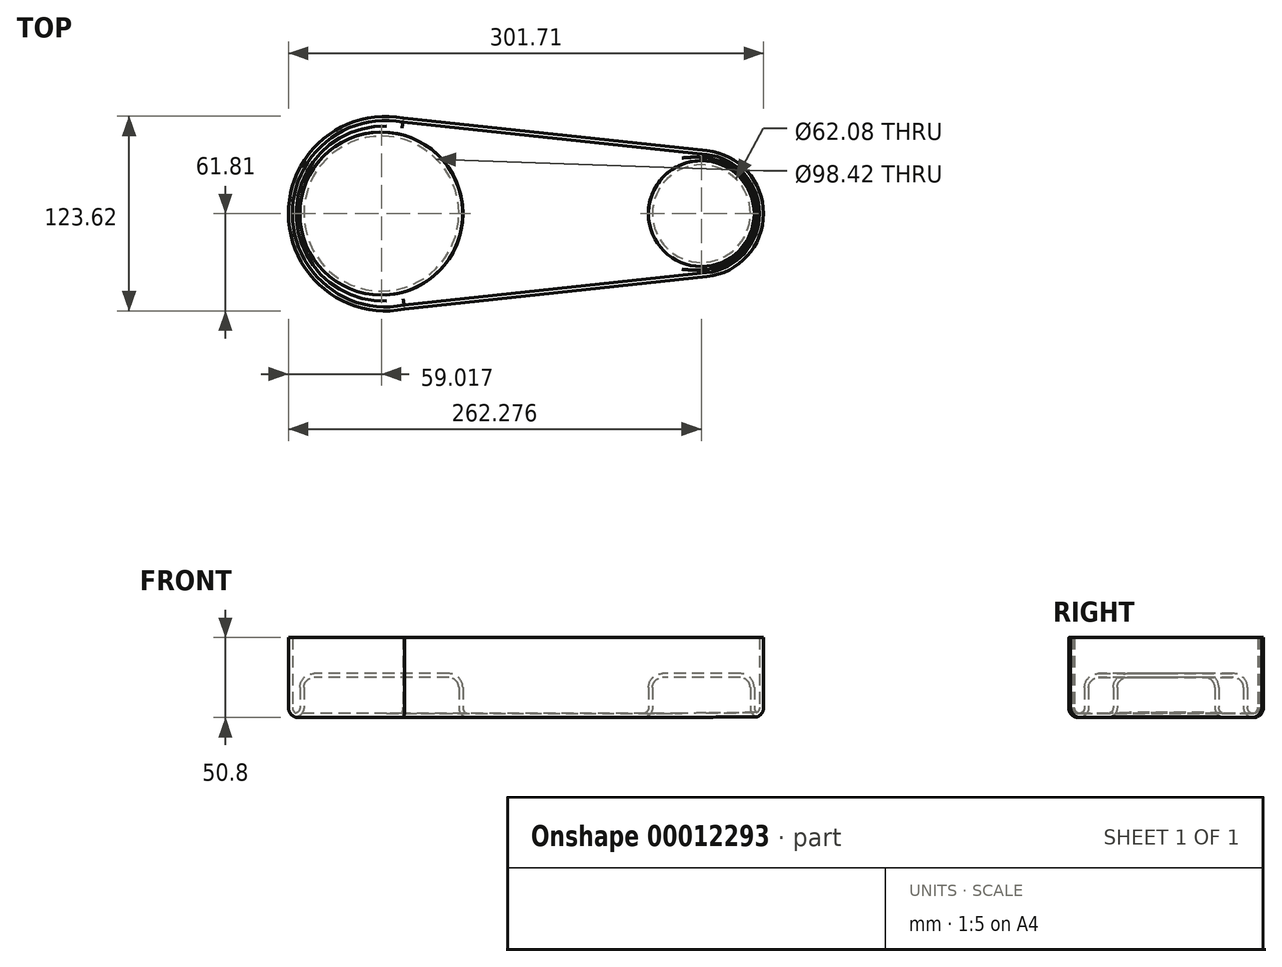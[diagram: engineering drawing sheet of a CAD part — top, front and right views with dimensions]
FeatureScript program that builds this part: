
annotation { "Feature Type Name" : "Feature", "Feature Type Description" : "" }
export const myFeature = defineFeature(function(context is Context, id is Id, definition is map)
    precondition{}
    {
        {
            var Q0;
            Q0=qCreatedBy(makeId("Top.planeOp"),FACE);
            var sketch = newSketch(context, id + "F0", { "sketchPlane" : qUnion([Q0])});
            skCircle(sketch, "E0", {"center": v(-77.5, 0) * mm, "radius": 61.81 * mm});
            skCircle(sketch, "E1", {"center": v(122.11, 0) * mm, "radius": 40.28 * mm});
            skLineSegment(sketch, "E2", {"start": v(-75.61, 61.78) * mm, "end": v(126.42, 40.05) * mm});
            skLineSegment(sketch, "E3", {"start": v(-76.43, -61.8) * mm, "end": v(126.4, -40.05) * mm});
            skSolve(sketch);
        }
        {
            var Q0;
            Q0 = qSketchRegion(id + "F0", true);
            extrude(context, id + "F1", {"entities" : qUnion([Q0]), "depth" : 50.8 * mm});
        }
        {
            var Q0;
            {var subQ1=sQuery(id+"F0.wireOp",EDGE,"E0");var subQ4=sQuery(id+"F0.wireOp",EDGE,"E2");var subQ6=makeQuery(id+"F0.imprint","INTERSECT",VERTEX,{"disambiguationData":[OD(0.0)],"derivedFrom":[subQ1,subQ4]});Q0=makeQuery(id+"F0.imprint","IMPRINT",FACE,{"disambiguationData":[TD([[makeQuery(id+"F0.imprint","IMPRINT",EDGE,{"disambiguationData":[TD([[subQ6,-1.0]])],"derivedFrom":subQ1}),1.0]])]});}
            var sketch = newSketch(context, id + "F2", { "sketchPlane" : qUnion([Q0])});
            skCircle(sketch, "E4", {"center": v(-80.3, 0) * mm, "radius": 49.2 * mm});
            skCircle(sketch, "E5", {"center": v(122.96, 0) * mm, "radius": 31.04 * mm});
            skSolve(sketch);
        }
        {
            var Q0;
            Q0=makeQuery(id+"F2.imprint","IMPRINT",FACE,{"disambiguationData":[TD([[makeQuery(id+"F2.imprint","IMPRINT",EDGE,{"derivedFrom":sQuery(id+"F2.wireOp",EDGE,"E4")}),1.0]])]});
            var Q1;
            Q1=makeQuery(id+"F2.imprint","IMPRINT",FACE,{"disambiguationData":[TD([[makeQuery(id+"F2.imprint","IMPRINT",EDGE,{"derivedFrom":sQuery(id+"F2.wireOp",EDGE,"E5")}),1.0]])]});
            extrude(context, id + "F3", {"entities" : qUnion([Q0, Q1]), "operationType" : NewBodyOperationType.REMOVE, "depth" : 25.4 * mm});
        }
        {
            var Q0;
            Q0=makeQuery(id+"F1.opExtrude","CAP_FACE",FACE,{"disambiguationData":[OSD([sQuery(id+"F0.wireOp",EDGE,"E0"),sQuery(id+"F0.wireOp",EDGE,"E1"),sQuery(id+"F0.wireOp",EDGE,"E2"),sQuery(id+"F0.wireOp",EDGE,"E3")])],"isStart":true});
            var Q1;
            Q1=makeQuery(id+"F3.boolean.opBoolean","COPY",FACE,{"derivedFrom":makeQuery(id+"F3.opExtrude","CAP_FACE",FACE,{"disambiguationData":[OSD([sQuery(id+"F2.wireOp",EDGE,"E4")])],"isStart":false})});
            var Q2;
            Q2=makeQuery(id+"F3.boolean.opBoolean","COPY",FACE,{"derivedFrom":makeQuery(id+"F3.opExtrude","CAP_FACE",FACE,{"disambiguationData":[OSD([sQuery(id+"F2.wireOp",EDGE,"E5")])],"isStart":false})});
            fillet(context, id + "F4", {"entities" : qUnion([Q0, Q1, Q2]), "radius" : 6.35 * mm, "tangentPropagation" : true, "allowEdgeOverflow" : false});
        }
        {
            var Q0;
            Q0=makeQuery(id+"F1.opExtrude","CAP_FACE",FACE,{"disambiguationData":[OSD([sQuery(id+"F0.wireOp",EDGE,"E0"),sQuery(id+"F0.wireOp",EDGE,"E1"),sQuery(id+"F0.wireOp",EDGE,"E2"),sQuery(id+"F0.wireOp",EDGE,"E3")])],"isStart":false});
            shell(context, id + "F5", {"entities" : qUnion([Q0]), "thickness" : 2.54 * mm});
        }
    });
